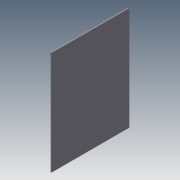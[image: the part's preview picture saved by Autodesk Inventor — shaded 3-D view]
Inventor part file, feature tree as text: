
AUTODESK INVENTOR PART (.ipt)
format: ipt  version: 2015 SP1 (Build 190203100, 203)  size: 68,096 bytes
history: native  units: mm
features: extrude x1, sketch x1
ambient origin geometry x8: Origin, YZ Plane, XZ Plane, XY Plane, X Axis, Y Axis, Z Axis, Center Point
bodies: Solid1 (feature_tree)
feature tree (2):
  extrude  "Extrusion1"  Depth=120.0mm
  sketch  "Sketch1"  dims[d0=160.0mm d1=120.0mm d2=1.5mm d3=0.0mm]
